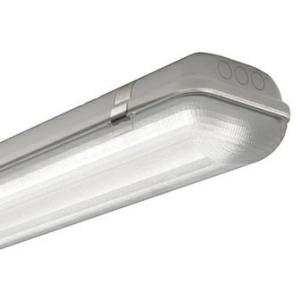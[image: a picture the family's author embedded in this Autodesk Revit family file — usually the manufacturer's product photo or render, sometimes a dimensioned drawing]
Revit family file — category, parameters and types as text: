
# Revit family: 3f_filippi_-_3f_linda_3f_filippi_-_58597_-_3f_linda_led_2x18w_l1270
name_source: partatom
category: Lighting Fixtures
units: mm (PartAtom-declared; Revit-internal decimal feet)

## family parameters
Cut with Voids When Loaded = No
Host = Face
Light Source = No
Part Type = Normal
Room Calculation Point = No
Round Connector Dimension = Use Diameter
Shared = No

## types (1)
- 3F Filippi - 3F Linda (1 x LED, 6048 lm, 40 W, 4000 K)
    Apparent Load = 40 VA
    Approval mark = CE
    CIE Flux Codes = 46 76 93 97 100
    Color Rendering = 80
    Color Temperature = 4000 K
    Control Gear = Electronic ballast
    Default Elevation = 1800 mm
    Description = ILLUMINOTECHNICAL
Luminous efficiency 100% (DLOR 97%, ULOR 3%).
Initial luminous flux of the luminaire 6048 lm.
Controlled symmetric distribution.
Installation Interdistance Transv.D = 1.52 x hu - Long.D = 1.17 x hu.
Tabular UGR (CIE 117 - 4H-8H; S=0.25H; 70/50/20): RUG 23.4 - 22.6.
Beam angle: 94° - 78°.
Luminous efficacy 151 lm/W.
Lifetime (L93/B10): 30000 h. (tq+25°C)
Lifetime (L90/B10): 50000 h. (tq+25°C)
Lifetime (L85/B10): 80000 h. (tq+25°C)
Lifetime (L80/B10): 100000 h. (tq+25°C)
Lifetime (L85/B10): 50000 h. (tq+40°C)
Sudden decreased luminous flux after 50000 hours: 0% (C0).
Photobiological safety in compliance with IEC/TR 62778: RG0 risk exempt, (IEC 62471).
In compliance with IEC/EN 62722-2-1 - IEC/EN 62717 standards.

SOURCE
2 linear LED modules 18W/840.
Energy efficiency class (UE 2019/2020 - UE 2019/2015): D.
CIE 13.3 Colour rendering index: CRI >80 (R9 <50%).
IES TM-30 Fidelity Index: Rf = 84 Rg = 95.
CCT nominal colour temperature 4000 K.
Colour initial tolerance (MacAdam): SDCM 3.

MECHANICAL
Self-extinguishing V2 polycarbonate housing, injection moulded, RAL 7035 grey.
Ecologic anti-aging injected sealing gasket.
Diffuser in self-extinguishing V2 polycarbonate, photo-engraved interior, UV stabilised, injection moulded with smooth outer surface, tamper-proof opening.
Gear-holder reflector in hot-dip galvanised steel, painted with white polyester base.
Snug fit safety snap-lock clips for diffuser mounting in stainless steel, screwdriver opening.
Fixing brackets in stainless steel.
Possibility for technicians to access the interior of the luminaire.
Luminaire with limited surface temperature. - D - (EN 60598-2-24)
Dimensions: 1270x160 mm, height 100 mm. Weight 2.78 kg.
IP66 protection degree.
Mechanical strength to impacts IK10 (20 joule).
Glow-wire test resistance 850°C.

ELECTRICAL
Halogen Free electronic wiring 230V-50/60Hz, power factor 0.95, THD <25%, constant output current, SELV, class I, 1 driver.
Power of the luminaire 40 W.
ENEC - CE.
SAFE FLICKER: PstLM=<1 and SVM=<0.4 (IEC TR 61547-1 and IEC TR 63158), to ensure a more comfortable and safe light.
Luminaire compliant with EN 60598-2-22 for power supply from a centralised emergency system CPSS (Central Power Supply System), not incorporated in the luminaire - high risk areas excluded. The default power and flux are 100% in AC and 100% in DC.
Ambient temperature from -20°C to +40°C.
Temperature class T6 max 85°C.
Relative humidity UR: <85%.

INSTALLATION
Ceiling / Suspended / Wall.
All accessories dedicated to this product are available on the Catalog and on our website www.3F-Filippi.com.

APPLICATIONS
Suitable product for food production plants (HACCP), IFS (Food Version 6), BRC (GSFS Food Version 7).
Dry, dusty indoor environments, subject to occasional water splashes.
Virtually shatterproof polycarbonate compatibly with the fumes / atmospheres that compromise the elasticity of plastic materials.
Not suitable for installation on surfaces subject to important vibrations, exposed to weather conditions, on ropes or poles.
Suitable for illumination of public car parks and parking grounds referred to DIN 67528:2018-04.

WARNING
Fixture not suitable for cold stores with an ambient temperature <0°C and/or relative humidity >85%.
Luminaire designed for disposal/recycling at end-of-life.
Replaceable (LED only) light source by a professional. Replaceable control gear by a professional.
    Height = 100 mm  [stored 0.328084 ft]
    Lamp = 1 x LED
    Lamp Light Flux = 6048 lm
    Lamp Power = 40 W
    Lamp count = 1
    Length = 1270 mm
    Lifetime = 50000 h
    Luminous efficacy = 151 lm/W
    Manufacturer = 3F Filippi
    ModVariant = No
    Model = 3F Filippi - 58597 - 3F Linda LED 2x18W L1270
    Mounting Place = Ceiling
    Mounting Type = Pendant
    Number of Poles = 1
    OnlyDefault = Yes
    Power Factor = 1
    Product Name = 3F Filippi - 3F Linda
    Product group = pendant luminaire
    ProductGroupID = 9
    Protection Class = Protection class I
    Protection Degree = IP 66
    RLX_Detail_Level = 1
    RLX_Emergency_Light_Flux = 0 lm
    RLX_Emergency_Type = 0
    RLX_Emergency_Type_DB = No
    RlxData = <blob elided: 71645 chars, md5=d4fdbde2>
    Socket = socket
    Standby Power = 0 W
    System Light Flux = 6048 lm
    System Power = 40 W
    Type Comments = Product without accessories
    Type Image = 3ffilippi_3f_linda_led_2x.jpg
    URL = http://relux.com
    VarID = ---
    Voltage = 0 V
    Weight = 0.00 kg
    Width = 160 mm

note: [stored X ft] marks values corroborated as IEEE doubles in the binary element streams (Revit-internal decimal feet)

## geometry (parser evidence)
native form markers: Blend x4, Sweep x9
no freeform markers — native parametric forms only
